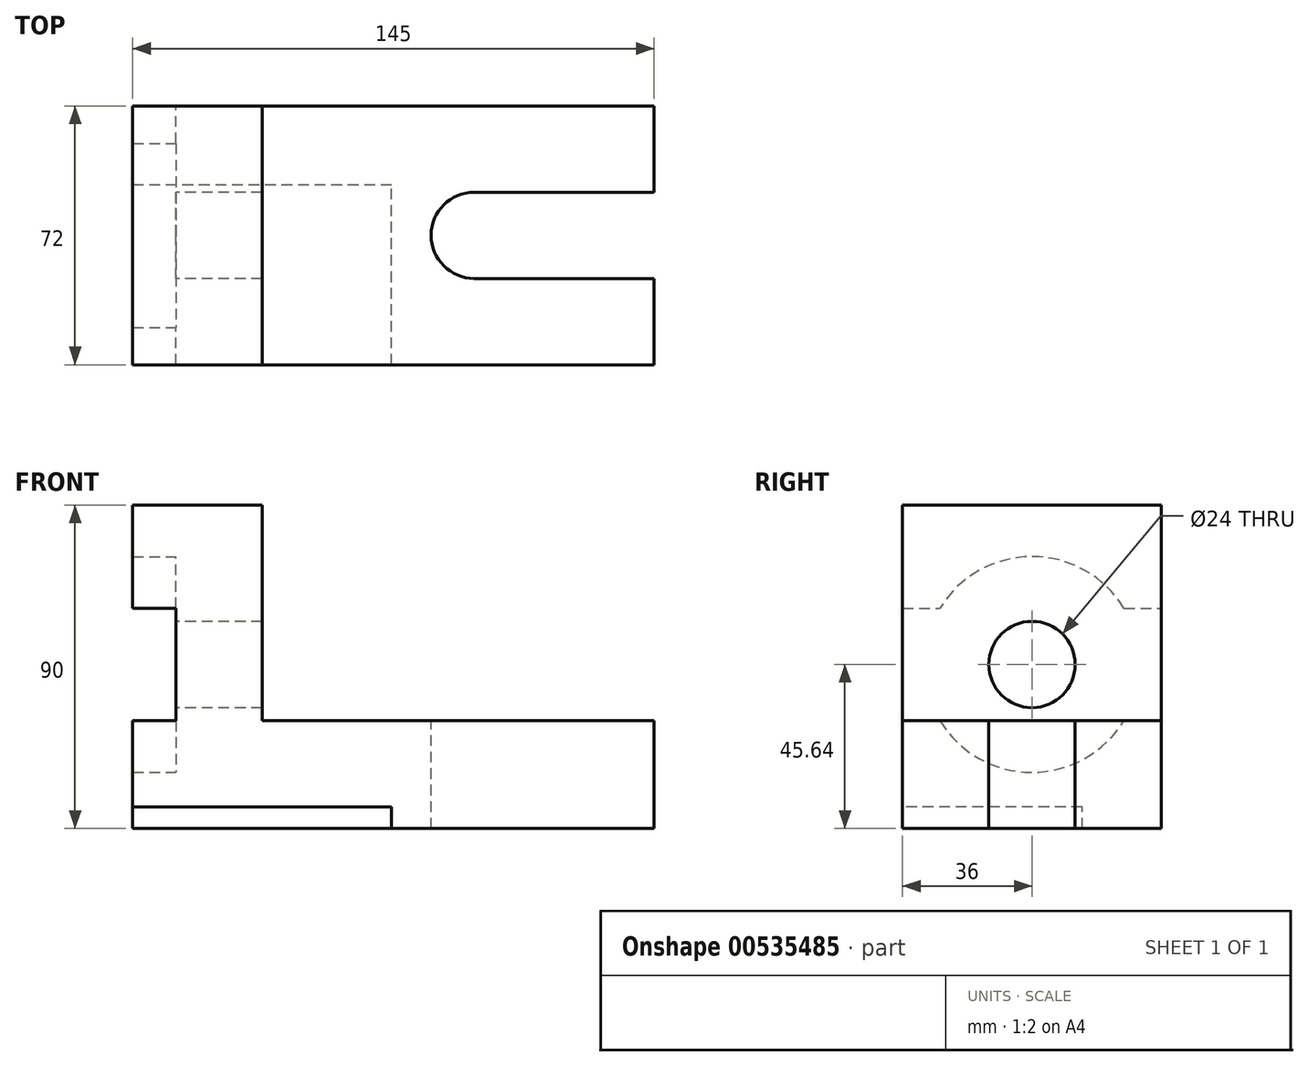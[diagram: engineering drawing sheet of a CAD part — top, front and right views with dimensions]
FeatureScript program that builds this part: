
annotation { "Feature Type Name" : "Feature", "Feature Type Description" : "" }
export const myFeature = defineFeature(function(context is Context, id is Id, definition is map)
    precondition{}
    {
        {
            var Q0;
            Q0=qCreatedBy(makeId("Front.planeOp"),FACE);
            var sketch = newSketch(context, id + "F0", { "sketchPlane" : qUnion([Q0])});
            skLineSegment(sketch, "E0", {"start": v(-81.8, 76.9) * mm, "end": v(-45.8, 76.9) * mm});
            skLineSegment(sketch, "E1", {"start": v(-45.8, 76.9) * mm, "end": v(-45.8, 16.9) * mm});
            skLineSegment(sketch, "E2", {"start": v(-45.8, 16.9) * mm, "end": v(63.2, 16.9) * mm});
            skLineSegment(sketch, "E3", {"start": v(63.2, 16.9) * mm, "end": v(63.2, -13.1) * mm});
            skLineSegment(sketch, "E4", {"start": v(63.2, -13.1) * mm, "end": v(-9.8, -13.1) * mm});
            skLineSegment(sketch, "E5", {"start": v(-9.8, -13.1) * mm, "end": v(-9.8, -13.1) * mm});
            skLineSegment(sketch, "E6", {"start": v(-9.8, -13.1) * mm, "end": v(-81.8, -13.1) * mm});
            skLineSegment(sketch, "E7", {"start": v(-81.8, -13.1) * mm, "end": v(-81.8, 16.9) * mm});
            skLineSegment(sketch, "E8", {"start": v(-81.8, 16.9) * mm, "end": v(-69.8, 16.9) * mm});
            skLineSegment(sketch, "E9", {"start": v(-69.8, 16.9) * mm, "end": v(-69.8, 48.16) * mm});
            skLineSegment(sketch, "E10", {"start": v(-69.8, 48.16) * mm, "end": v(-81.8, 48.16) * mm});
            skLineSegment(sketch, "E11", {"start": v(-81.8, 48.16) * mm, "end": v(-81.8, 76.9) * mm});
            skSolve(sketch);
        }
        {
            var Q0;
            Q0=makeQuery(id+"F0.imprint","IMPRINT",FACE,{"disambiguationData":[TD([[makeQuery(id+"F0.imprint","IMPRINT",EDGE,{"derivedFrom":sQuery(id+"F0.wireOp",EDGE,"E0")}),-1.0]])]});
            extrude(context, id + "F1", {"entities" : qUnion([Q0]), "depth" : 72 * mm, "offsetDistance" : 25 * mm});
        }
        {
            var Q0;
            Q0=makeQuery(id+"F1.opExtrude","SWEPT_FACE",FACE,{"disambiguationData":[OSD([sQuery(id+"F0.wireOp",EDGE,"E2")])]});
            var sketch = newSketch(context, id + "F2", { "sketchPlane" : qUnion([Q0])});
            skArc(sketch, "E12", {"start": v(13.2, -24) * mm, "mid": v(1.2, -36) * mm, "end": v(13.2, -48) * mm});
            skPoint(sketch, "E12.centerSnap0", {"position": v(63.2, -36) * mm});
            skLineSegment(sketch, "E13", {"start": v(63.2, -24) * mm, "end": v(13.2, -24) * mm});
            skLineSegment(sketch, "E14", {"start": v(63.2, -48) * mm, "end": v(13.2, -48) * mm});
            skLineSegment(sketch, "E15", {"start": v(63.2, -24) * mm, "end": v(63.2, -48) * mm});
            skSolve(sketch);
        }
        {
            var Q0;
            Q0 = qSketchRegion(id + "F2", true);
            extrude(context, id + "F3", {"entities" : qUnion([Q0]), "operationType" : NewBodyOperationType.REMOVE, "endBound" : BoundingType.THROUGH_ALL, "oppositeDirection" : true, "depth" : 25 * mm, "offsetDistance" : 25 * mm});
        }
        {
            var Q0;
            Q0=makeQuery(id+"F1.opExtrude","SWEPT_FACE",FACE,{"disambiguationData":[OSD([sQuery(id+"F0.wireOp",EDGE,"E9")])]});
            var sketch = newSketch(context, id + "F4", { "sketchPlane" : qUnion([Q0])});
            skLineSegment(sketch, "E16", {"start": v(36, 76.96) * mm, "end": v(36, -9.52) * mm, "construction": true});
            skPoint(sketch, "E16.startSnap0", {"position": v(36, 48.16) * mm});
            skPoint(sketch, "E16.endSnap0", {"position": v(36, 16.9) * mm});
            skLineSegment(sketch, "E17", {"start": v(0, 32.53) * mm, "end": v(72, 32.53) * mm, "construction": true});
            skCircle(sketch, "E18", {"center": v(36, 32.53) * mm, "radius": 12 * mm});
            skArc(sketch, "E19", {"start": v(10.4, 16.9) * mm, "mid": v(36, 2.53) * mm, "end": v(61.6, 16.9) * mm});
            skLineSegment(sketch, "E20", {"start": v(61.6, 48.16) * mm, "end": v(72, 48.16) * mm});
            skLineSegment(sketch, "E21", {"start": v(61.6, 16.9) * mm, "end": v(72, 16.9) * mm});
            skLineSegment(sketch, "E22", {"start": v(10.4, 16.9) * mm, "end": v(0, 16.9) * mm});
            skLineSegment(sketch, "E23", {"start": v(10.4, 48.16) * mm, "end": v(0, 48.16) * mm});
            skArc(sketch, "E24.trimOffspring", {"start": v(61.6, 48.16) * mm, "mid": v(36, 62.53) * mm, "end": v(10.4, 48.16) * mm});
            skLineSegment(sketch, "E25", {"start": v(10.4, 48.16) * mm, "end": v(61.6, 48.16) * mm});
            skLineSegment(sketch, "E26", {"start": v(10.4, 16.9) * mm, "end": v(61.6, 16.9) * mm});
            skSolve(sketch);
        }
        {
            var Q0;
            Q0=makeQuery(id+"F1.opExtrude","SWEPT_FACE",FACE,{"disambiguationData":[OSD([sQuery(id+"F0.wireOp",EDGE,"E7")])]});
            var sketch = newSketch(context, id + "F5", { "sketchPlane" : qUnion([Q0])});
            skLineSegment(sketch, "E27", {"start": v(22, -13.1) * mm, "end": v(22, -7.1) * mm});
            skLineSegment(sketch, "E28", {"start": v(22, -7.1) * mm, "end": v(72, -7.1) * mm});
            skSolve(sketch);
        }
        {
            var Q0;
            Q0 = qSketchRegion(id + "F5", true);
            var Q1;
            {var subQ0=sQuery(id+"F5.wireOp",EDGE,"E27");Q1=makeQuery(id+"F5.imprint","IMPRINT",FACE,{"disambiguationData":[TD([[makeQuery(id+"F5.imprint","IMPRINT",EDGE,{"derivedFrom":subQ0}),-1.0]])]});}
            extrude(context, id + "F6", {"entities" : qUnion([Q0, Q1]), "operationType" : NewBodyOperationType.REMOVE, "oppositeDirection" : true, "depth" : 72 * mm, "offsetDistance" : 25 * mm});
        }
        {
            var Q0;
            Q0=makeQuery(id+"F4.imprint","IMPRINT",FACE,{"disambiguationData":[TD([[makeQuery(id+"F4.imprint","IMPRINT",EDGE,{"derivedFrom":sQuery(id+"F4.wireOp",EDGE,"E18")}),1.0]])]});
            extrude(context, id + "F7", {"entities" : qUnion([Q0]), "operationType" : NewBodyOperationType.REMOVE, "endBound" : BoundingType.THROUGH_ALL, "oppositeDirection" : true, "depth" : 25 * mm, "offsetDistance" : 25 * mm});
        }
        {
            var Q0;
            Q0 = qSketchRegion(id + "F4", true);
            extrude(context, id + "F8", {"entities" : qUnion([Q0]), "operationType" : NewBodyOperationType.REMOVE, "endBound" : BoundingType.THROUGH_ALL, "depth" : 12 * mm, "offsetDistance" : 25 * mm});
        }
    });
